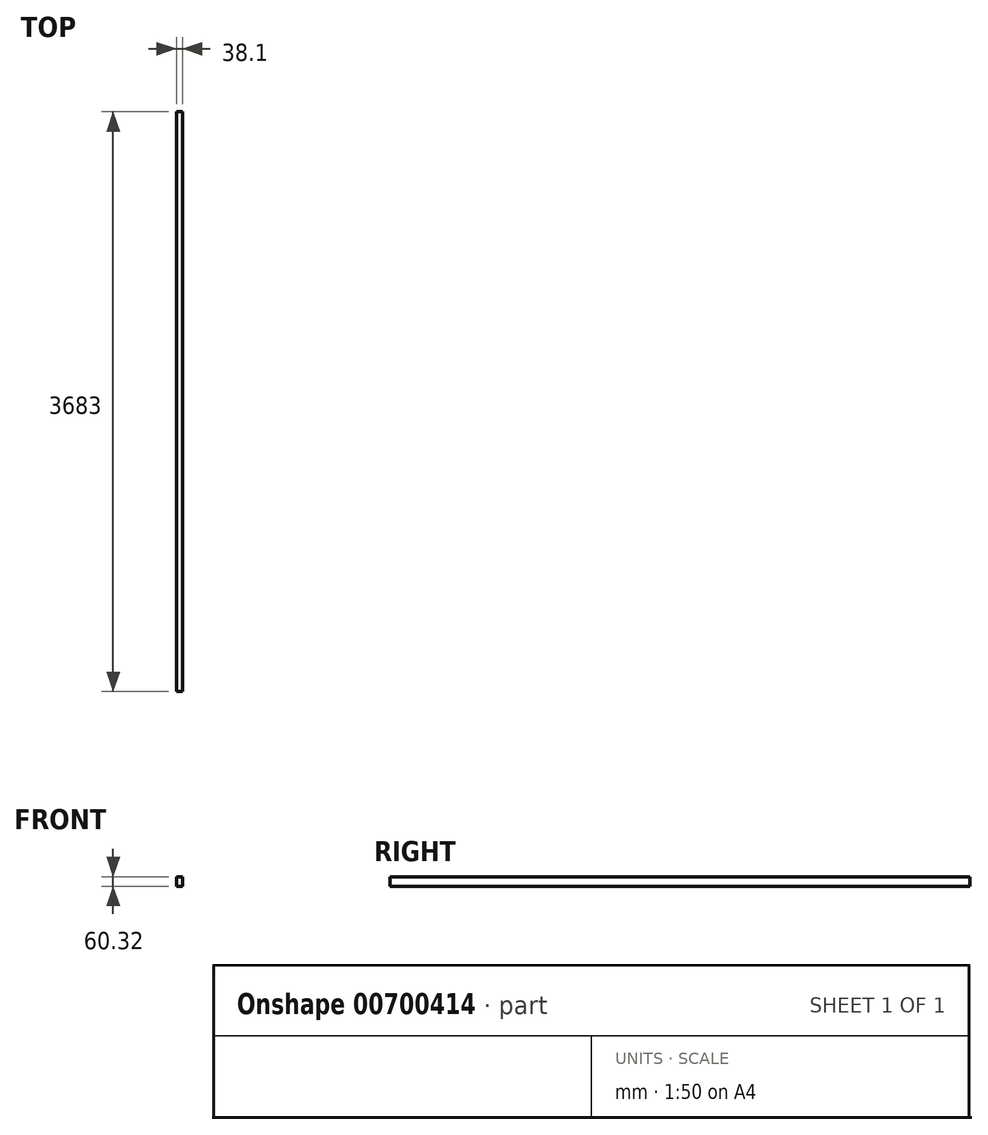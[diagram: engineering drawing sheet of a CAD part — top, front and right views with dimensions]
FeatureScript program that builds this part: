
annotation { "Feature Type Name" : "Feature", "Feature Type Description" : "" }
export const myFeature = defineFeature(function(context is Context, id is Id, definition is map)
    precondition{}
    {
        {
            var Q0;
            Q0=qCreatedBy(makeId("Front.planeOp"),FACE);
            var sketch = newSketch(context, id + "F0", { "sketchPlane" : qUnion([Q0])});
            skLineSegment(sketch, "E0.bottom", {"start": v(-19.05, 30.16) * mm, "end": v(19.05, 30.16) * mm});
            skLineSegment(sketch, "E0.top", {"start": v(-19.05, -30.16) * mm, "end": v(19.05, -30.16) * mm});
            skLineSegment(sketch, "E0.left", {"start": v(-19.05, 30.16) * mm, "end": v(-19.05, -30.16) * mm});
            skLineSegment(sketch, "E0.right", {"start": v(19.05, 30.16) * mm, "end": v(19.05, -30.16) * mm});
            skLineSegment(sketch, "E1", {"start": v(-19.05, 30.16) * mm, "end": v(19.05, -30.16) * mm, "construction": true});
            skSolve(sketch);
        }
        {
            var Q0;
            Q0=qSketchRegion(id+"F0",true);
            extrude(context, id + "F1", {"entities" : qUnion([Q0]), "endBound" : BoundingType.SYMMETRIC, "depth" : 3683 * mm, "offsetDistance" : 25.4 * mm});
        }
    });
